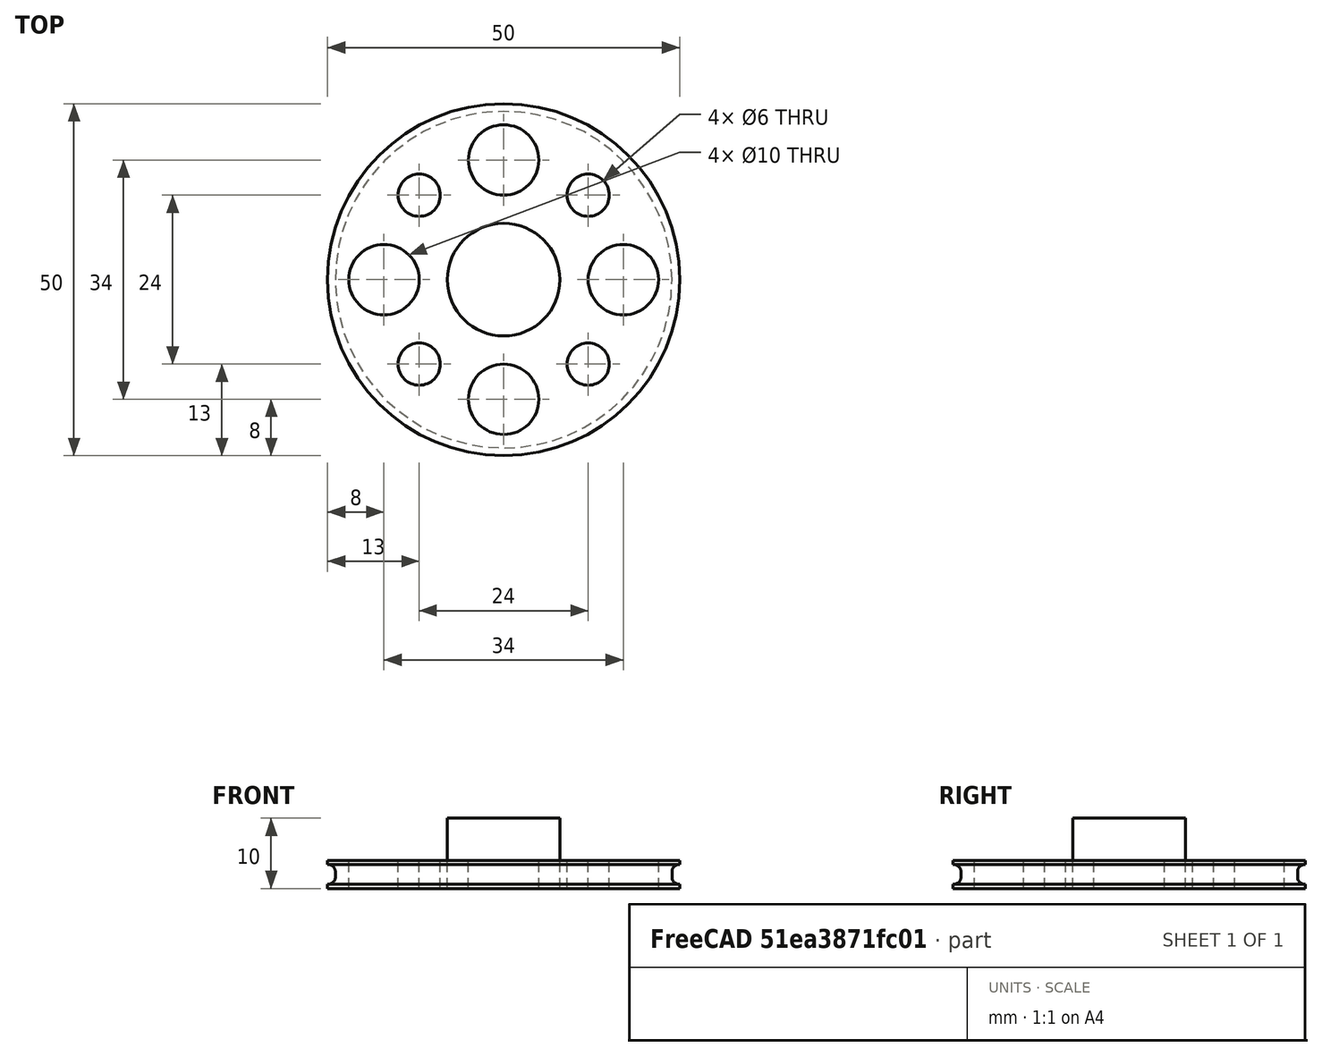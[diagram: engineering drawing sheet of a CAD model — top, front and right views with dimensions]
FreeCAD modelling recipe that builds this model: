
FCSTD DOCUMENT  (FreeCAD 0.18.4R)
Label: ruedas_sin_soporte
License: All rights reserved
LicenseURL: http://en.wikipedia.org/wiki/All_rights_reserved
objects: Part::Cylinder×12, Part::Cut×10, Part::Fillet×1
note: 23 computed .brp shape members not serialized (recipe doc carries the construction recipe); baked Part::Feature solids carry a one-line shape summary decoded from their .brp

FEATURE [Part::Cylinder] Cylinder  label="Cilindro"
  Angle = 360
  AttacherType = Attacher::AttachEngine3D
  Height = 4
  Radius = 25
FEATURE [Part::Cylinder] Cylinder001  label="Cilindro001"
  Angle = 360
  AttacherType = Attacher::AttachEngine3D
  Height = 10
  Radius = 8
FEATURE [Part::Cylinder] Cylinder002  label="Cilindro002"
  Angle = 360
  AttacherType = Attacher::AttachEngine3D
  Height = 15
  Placement = pos=(17,0,-2) rot=(0,0,1;0rad)
  Radius = 5
FEATURE [Part::Cylinder] Cylinder003  label="Cilindro003"
  Angle = 360
  AttacherType = Attacher::AttachEngine3D
  Height = 15
  Placement = pos=(-17,0,-2) rot=(0,0,1;0rad)
  Radius = 5
FEATURE [Part::Cylinder] Cylinder004  label="Cilindro004"
  Angle = 360
  AttacherType = Attacher::AttachEngine3D
  Height = 15
  Placement = pos=(0,17,-2) rot=(0,0,1;0rad)
  Radius = 5
FEATURE [Part::Cylinder] Cylinder005  label="Cilindro005"
  Angle = 360
  AttacherType = Attacher::AttachEngine3D
  Height = 15
  Placement = pos=(0,-17,-2) rot=(0,0,1;0rad)
  Radius = 5
FEATURE [Part::Cylinder] Cylinder006  label="Cilindro006"
  Angle = 360
  AttacherType = Attacher::AttachEngine3D
  Height = 10
  Placement = pos=(-12,-12,-2) rot=(0,0,1;0rad)
  Radius = 3
FEATURE [Part::Cylinder] Cylinder007  label="Cilindro007"
  Angle = 360
  AttacherType = Attacher::AttachEngine3D
  Height = 10
  Placement = pos=(-12,12,-2) rot=(0,0,1;0rad)
  Radius = 3
FEATURE [Part::Cylinder] Cylinder008  label="Cilindro008"
  Angle = 360
  AttacherType = Attacher::AttachEngine3D
  Height = 10
  Placement = pos=(12,-12,-2) rot=(0,0,1;0rad)
  Radius = 3
FEATURE [Part::Cylinder] Cylinder009  label="Cilindro009"
  Angle = 360
  AttacherType = Attacher::AttachEngine3D
  Height = 10
  Placement = pos=(12,12,-2) rot=(0,0,1;0rad)
  Radius = 3
FEATURE [Part::Cut] Cut
  Base = -> Cylinder
  Tool = -> Cylinder004
FEATURE [Part::Cut] Cut001
  Base = -> Cut
  Tool = -> Cylinder007
FEATURE [Part::Cut] Cut002
  Base = -> Cut001
  Tool = -> Cylinder003
FEATURE [Part::Cut] Cut003
  Base = -> Cut002
  Tool = -> Cylinder006
FEATURE [Part::Cut] Cut004
  Base = -> Cut003
  Tool = -> Cylinder005
FEATURE [Part::Cut] Cut005
  Base = -> Cut004
  Tool = -> Cylinder008
FEATURE [Part::Cut] Cut006
  Base = -> Cut005
  Tool = -> Cylinder002
FEATURE [Part::Cut] Cut007
  Base = -> Cut006
  Tool = -> Cylinder009
FEATURE [Part::Cylinder] Cylinder010  label="Cilindro010"
  Angle = 360
  AttacherType = Attacher::AttachEngine3D
  Height = 2.8
  Placement = pos=(0,0,0.6) rot=(0,0,1;0rad)
  Radius = 25
FEATURE [Part::Cylinder] Cylinder011  label="Cilindro011"
  Angle = 360
  AttacherType = Attacher::AttachEngine3D
  Height = 2.8
  Placement = pos=(0,0,0.6) rot=(0,0,1;0rad)
  Radius = 23.9
FEATURE [Part::Cut] Cut008
  Base = -> Cylinder010
  Tool = -> Cylinder011
FEATURE [Part::Cut] Cut009
  Base = -> Cut007
  Tool = -> Cut008
FEATURE [Part::Fillet] Fillet
  Base = -> Cut009
  Edges = 2 edges r=1: [Edge4,Edge14]
